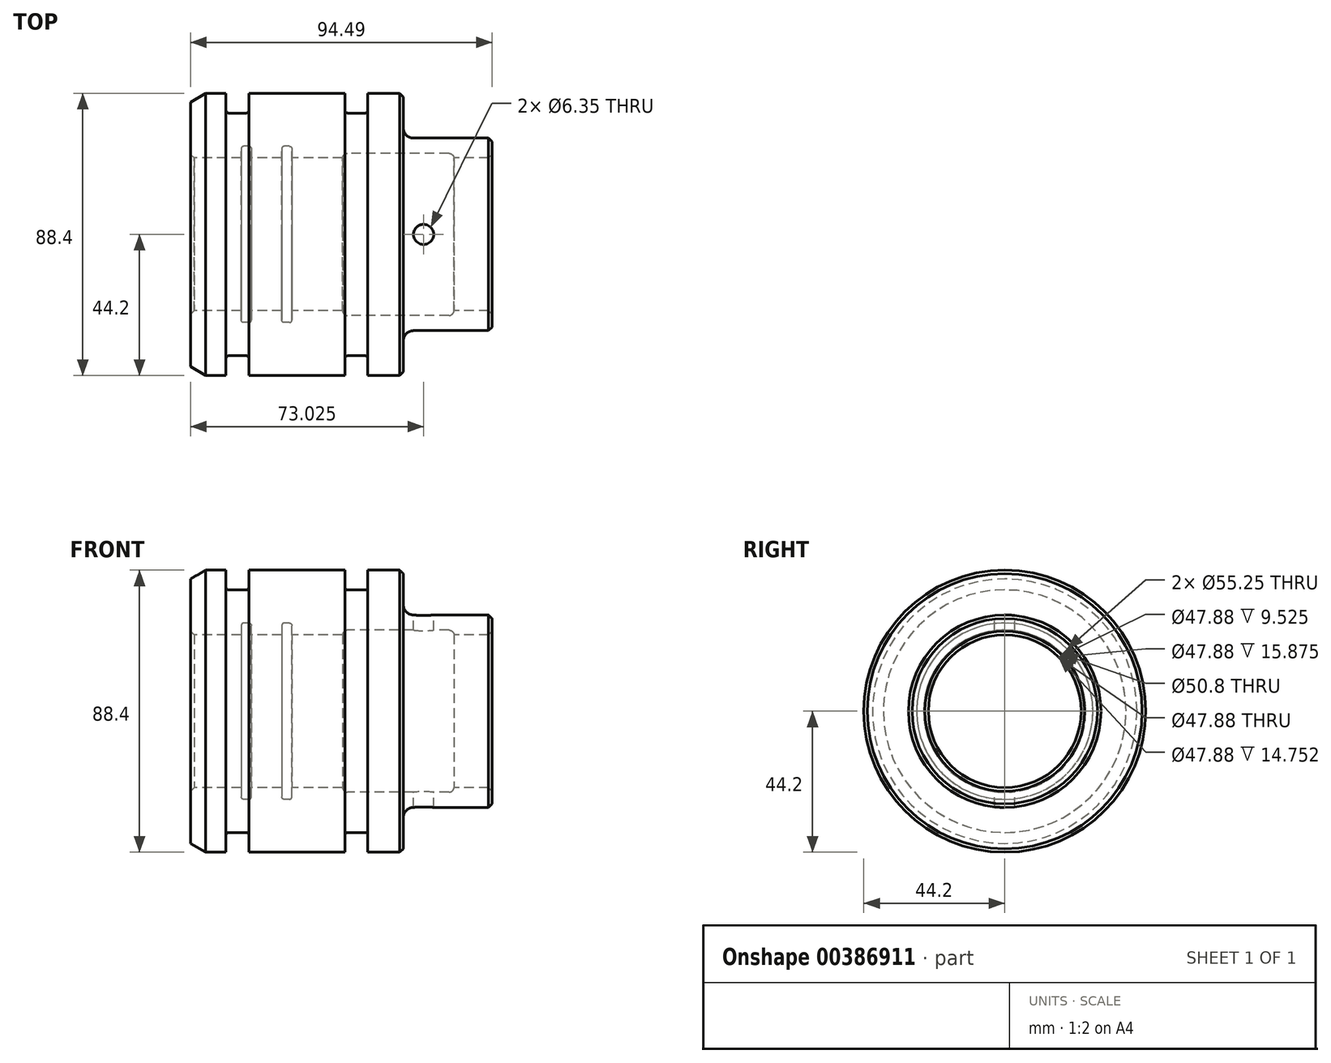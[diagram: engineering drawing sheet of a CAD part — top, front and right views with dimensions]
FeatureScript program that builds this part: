
annotation { "Feature Type Name" : "Feature", "Feature Type Description" : "" }
export const myFeature = defineFeature(function(context is Context, id is Id, definition is map)
    precondition{}
    {
        {
            var Q0;
            Q0=qCreatedBy(makeId("Front.planeOp"),FACE);
            var sketch = newSketch(context, id + "F0", { "sketchPlane" : qUnion([Q0])});
            skLineSegment(sketch, "E0", {"start": v(0, 0) * mm, "end": v(111.33, 0) * mm, "construction": true});
            skLineSegment(sketch, "E1", {"start": v(1.12, 23.94) * mm, "end": v(15.88, 23.94) * mm});
            skLineSegment(sketch, "E2", {"start": v(15.88, 23.94) * mm, "end": v(15.88, 27.62) * mm});
            skLineSegment(sketch, "E3", {"start": v(15.88, 27.62) * mm, "end": v(19.05, 27.62) * mm});
            skLineSegment(sketch, "E4", {"start": v(19.05, 27.62) * mm, "end": v(19.05, 23.94) * mm});
            skLineSegment(sketch, "E5", {"start": v(19.05, 23.94) * mm, "end": v(28.58, 23.94) * mm});
            skLineSegment(sketch, "E6", {"start": v(28.58, 23.94) * mm, "end": v(28.58, 27.62) * mm});
            skLineSegment(sketch, "E7", {"start": v(28.58, 27.62) * mm, "end": v(31.75, 27.62) * mm});
            skLineSegment(sketch, "E8", {"start": v(31.75, 27.62) * mm, "end": v(31.75, 23.94) * mm});
            skLineSegment(sketch, "E9", {"start": v(31.75, 23.94) * mm, "end": v(47.63, 23.94) * mm});
            skLineSegment(sketch, "E10", {"start": v(47.63, 23.94) * mm, "end": v(47.63, 25.4) * mm});
            skLineSegment(sketch, "E11", {"start": v(47.63, 25.4) * mm, "end": v(82.55, 25.4) * mm});
            skLineSegment(sketch, "E12", {"start": v(82.55, 25.4) * mm, "end": v(82.55, 23.94) * mm});
            skLineSegment(sketch, "E13", {"start": v(82.55, 23.94) * mm, "end": v(93.37, 23.94) * mm});
            skLineSegment(sketch, "E14", {"start": v(94.49, 25.06) * mm, "end": v(94.49, 29.04) * mm});
            skLineSegment(sketch, "E15", {"start": v(93.37, 30.16) * mm, "end": v(66.67, 30.16) * mm});
            skLineSegment(sketch, "E16", {"start": v(66.68, 30.16) * mm, "end": v(66.68, 43.07) * mm});
            skLineSegment(sketch, "E17", {"start": v(65.55, 44.2) * mm, "end": v(55.56, 44.2) * mm});
            skLineSegment(sketch, "E18", {"start": v(55.56, 44.2) * mm, "end": v(55.56, 38.02) * mm});
            skLineSegment(sketch, "E19", {"start": v(55.56, 38.02) * mm, "end": v(48.43, 38.02) * mm});
            skLineSegment(sketch, "E20", {"start": v(48.43, 38.02) * mm, "end": v(48.43, 44.2) * mm});
            skLineSegment(sketch, "E21", {"start": v(48.43, 44.2) * mm, "end": v(18.25, 44.2) * mm});
            skLineSegment(sketch, "E22", {"start": v(18.25, 44.2) * mm, "end": v(18.25, 38.02) * mm});
            skLineSegment(sketch, "E23", {"start": v(18.25, 38.02) * mm, "end": v(11.11, 38.02) * mm});
            skLineSegment(sketch, "E24", {"start": v(11.11, 38.02) * mm, "end": v(11.11, 44.2) * mm});
            skLineSegment(sketch, "E25", {"start": v(11.11, 44.2) * mm, "end": v(4.76, 44.2) * mm});
            skLineSegment(sketch, "E26", {"start": v(4.76, 44.2) * mm, "end": v(0, 41.45) * mm});
            skLineSegment(sketch, "E27", {"start": v(0, 41.45) * mm, "end": v(0, 25.06) * mm});
            skLineSegment(sketch, "E28", {"start": v(93.37, 23.94) * mm, "end": v(94.49, 25.06) * mm});
            skLineSegment(sketch, "E29", {"start": v(93.37, 30.16) * mm, "end": v(94.5, 29.04) * mm});
            skLineSegment(sketch, "E30", {"start": v(65.55, 44.2) * mm, "end": v(66.68, 43.07) * mm});
            skLineSegment(sketch, "E31", {"start": v(0, 25.06) * mm, "end": v(1.12, 23.94) * mm});
            skPoint(sketch, "E32.orphan", {"position": v(0, 23.94) * mm});
            skSolve(sketch);
        }
        {
            var Q0;
            Q0=qSketchRegion(id+"F0",true);
            var Q1;
            Q1=sQuery(id+"F0.wireOp",EDGE,"E0");
            revolve(context, id + "F1", {"entities" : qUnion([Q0]), "axis" : qUnion([Q1]), "revolveType" : RevolveType.FULL});
        }
        {
            var Q0;
            Q0=makeQuery(id+"F1.opRevolve","SWEPT_EDGE",EDGE,{"disambiguationData":[OSD([sQuery(id+"F0.wireOp",EDGE,"E15"),sQuery(id+"F0.wireOp",EDGE,"E16")])]});
            fillet(context, id + "F2", {"entities" : qUnion([Q0]), "radius" : 3.17 * mm, "tangentPropagation" : true, "allowEdgeOverflow" : false});
        }
        {
            var Q0;
            Q0=makeQuery(id+"F1.opRevolve","SWEPT_EDGE",EDGE,{"disambiguationData":[OSD([sQuery(id+"F0.wireOp",EDGE,"E10"),sQuery(id+"F0.wireOp",EDGE,"E11")])]});
            var Q1;
            Q1=makeQuery(id+"F1.opRevolve","SWEPT_EDGE",EDGE,{"disambiguationData":[OSD([sQuery(id+"F0.wireOp",EDGE,"E11"),sQuery(id+"F0.wireOp",EDGE,"E12")])]});
            fillet(context, id + "F3", {"entities" : qUnion([Q0, Q1]), "radius" : 1.59 * mm, "tangentPropagation" : true, "allowEdgeOverflow" : false});
        }
        {
            var Q0;
            Q0=makeQuery(id+"F1.opRevolve","SWEPT_EDGE",EDGE,{"disambiguationData":[OSD([sQuery(id+"F0.wireOp",EDGE,"E22"),sQuery(id+"F0.wireOp",EDGE,"E23")])]});
            var Q1;
            Q1=makeQuery(id+"F1.opRevolve","SWEPT_EDGE",EDGE,{"disambiguationData":[OSD([sQuery(id+"F0.wireOp",EDGE,"E18"),sQuery(id+"F0.wireOp",EDGE,"E19")])]});
            var Q2;
            Q2=makeQuery(id+"F1.opRevolve","SWEPT_EDGE",EDGE,{"disambiguationData":[OSD([sQuery(id+"F0.wireOp",EDGE,"E3"),sQuery(id+"F0.wireOp",EDGE,"E4")])]});
            var Q3;
            Q3=makeQuery(id+"F1.opRevolve","SWEPT_EDGE",EDGE,{"disambiguationData":[OSD([sQuery(id+"F0.wireOp",EDGE,"E7"),sQuery(id+"F0.wireOp",EDGE,"E8")])]});
            var Q4;
            Q4=makeQuery(id+"F1.opRevolve","SWEPT_EDGE",EDGE,{"disambiguationData":[OSD([sQuery(id+"F0.wireOp",EDGE,"E2"),sQuery(id+"F0.wireOp",EDGE,"E3")])]});
            var Q5;
            Q5=makeQuery(id+"F1.opRevolve","SWEPT_EDGE",EDGE,{"disambiguationData":[OSD([sQuery(id+"F0.wireOp",EDGE,"E6"),sQuery(id+"F0.wireOp",EDGE,"E7")])]});
            var Q6;
            Q6=makeQuery(id+"F1.opRevolve","SWEPT_EDGE",EDGE,{"disambiguationData":[OSD([sQuery(id+"F0.wireOp",EDGE,"E23"),sQuery(id+"F0.wireOp",EDGE,"E24")])]});
            var Q7;
            Q7=makeQuery(id+"F1.opRevolve","SWEPT_EDGE",EDGE,{"disambiguationData":[OSD([sQuery(id+"F0.wireOp",EDGE,"E19"),sQuery(id+"F0.wireOp",EDGE,"E20")])]});
            fillet(context, id + "F4", {"entities" : qUnion([Q0, Q1, Q2, Q3, Q4, Q5, Q6, Q7]), "radius" : 0.8 * mm, "tangentPropagation" : true, "allowEdgeOverflow" : false});
        }
        {
            var Q0;
            Q0=qCreatedBy(makeId("Top.planeOp"),FACE);
            var sketch = newSketch(context, id + "F5", { "sketchPlane" : qUnion([Q0])});
            skCircle(sketch, "E33", {"center": v(73.03, 0) * mm, "radius": 3.18 * mm});
            skSolve(sketch);
        }
        {
            var Q0;
            Q0=qSketchRegion(id+"F5",true);
            extrude(context, id + "F6", {"entities" : qUnion([Q0]), "operationType" : NewBodyOperationType.REMOVE, "oppositeDirection" : true, "depth" : 101.6 * mm, "offsetDistance" : 25.4 * mm, "symmetric" : true});
        }
    });
